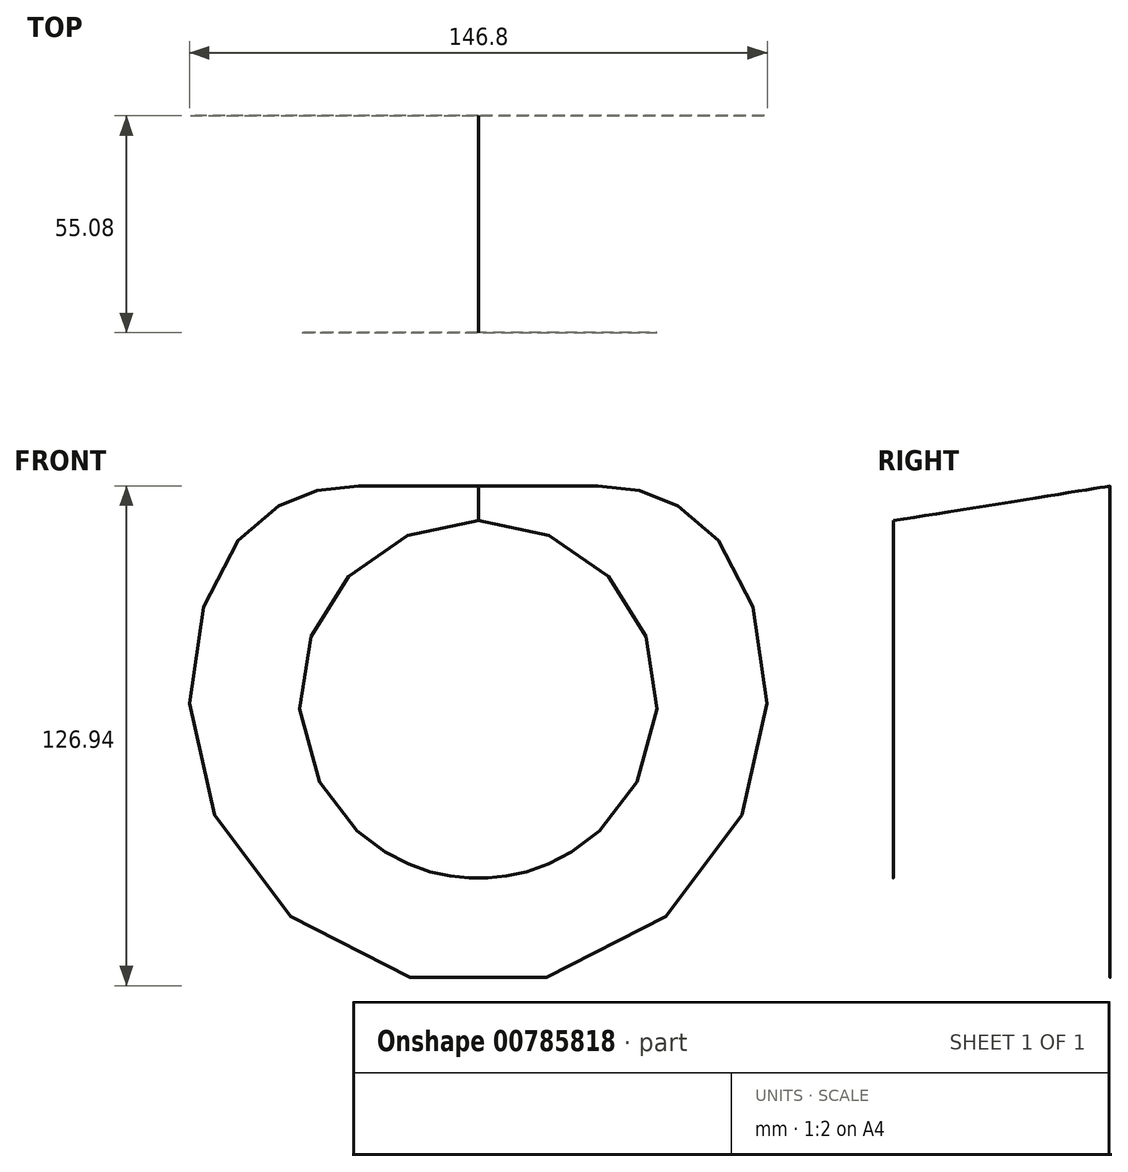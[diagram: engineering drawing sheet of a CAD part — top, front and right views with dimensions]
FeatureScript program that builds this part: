
annotation { "Feature Type Name" : "Feature", "Feature Type Description" : "" }
export const myFeature = defineFeature(function(context is Context, id is Id, definition is map)
    precondition{}
    {
        {
            var Q0;
            Q0=qCreatedBy(makeId("Front.planeOp"),FACE);
            cPlane(context, id + "F0", {"entities" : qUnion([Q0]), "cplaneType" : CPlaneType.OFFSET, "offset" : 50.8 * mm, "width" : 152.4 * mm, "height" : 152.4 * mm});
        }
        {
            var Q0;
            Q0=qCreatedBy(id+"F0.planeOp",FACE);
            var Q1;
            Q1 = qBodyType(qCreatedBy(id + "F2" ,EDGE), BodyType.WIRE);
            cPlane(context, id + "F1", {"entities" : qUnion([Q0, Q1]), "cplaneType" : CPlaneType.OFFSET, "offset" : 50.8 * mm, "width" : 152.4 * mm, "height" : 152.4 * mm});
        }
        {
            var Q0;
            Q0=qCreatedBy(id+"F1.planeOp",FACE);
            var sketch = newSketch(context, id + "F2", { "sketchPlane" : qUnion([Q0])});
            skCircle(sketch, "E0", {"center": v(0, 0) * mm, "radius": 91.15 * mm});
            skSolve(sketch);
        }
        {
            var Q0;
            Q0=qCreatedBy(id+"F1.planeOp",FACE);
            cPlane(context, id + "F3", {"entities" : qUnion([Q0]), "cplaneType" : CPlaneType.OFFSET, "offset" : 57.15 * mm, "width" : 152.4 * mm, "height" : 152.4 * mm});
        }
        {
            var Q0;
            Q0=qCreatedBy(id+"F3.planeOp",FACE);
            var sketch = newSketch(context, id + "F4", { "sketchPlane" : qUnion([Q0])});
            skArc(sketch, "E1", {"start": v(-65.98, 32.11) * mm, "mid": v(0, -73.38) * mm, "end": v(65.98, 32.11) * mm});
            skLineSegment(sketch, "E2", {"start": v(-31.72, 53.54) * mm, "end": v(0, 53.54) * mm});
            skLineSegment(sketch, "E3.MirrorCS", {"start": v(31.72, 53.54) * mm, "end": v(0, 53.54) * mm});
            skPoint(sketch, "E4.visualSharp", {"position": v(-50.18, 53.54) * mm});
            skArc(sketch, "E4.filletArc", {"start": v(-31.72, 53.54) * mm, "mid": v(-51.93, 47.74) * mm, "end": v(-65.98, 32.11) * mm});
            skPoint(sketch, "E5", {"position": v(50.18, 53.54) * mm});
            skArc(sketch, "E6.filletArc", {"start": v(65.98, 32.11) * mm, "mid": v(51.93, 47.74) * mm, "end": v(31.72, 53.54) * mm});
            skSolve(sketch);
        }
        {
            var Q0;
            Q0=qCreatedBy(id+"F3.planeOp",FACE);
            cPlane(context, id + "F5", {"entities" : qUnion([Q0]), "cplaneType" : CPlaneType.OFFSET, "offset" : 50.8 * mm, "width" : 152.4 * mm, "height" : 152.4 * mm});
        }
        {
            var Q0;
            Q0=qCreatedBy(id+"F5.planeOp",FACE);
            var sketch = newSketch(context, id + "F6", { "sketchPlane" : qUnion([Q0])});
            skCircle(sketch, "E7", {"center": v(0, 0) * mm, "radius": 45.44 * mm});
            skSolve(sketch);
        }
        {
            var Q0;
            Q0=qCreatedBy(id+"F5.planeOp",FACE);
            cPlane(context, id + "F7", {"entities" : qUnion([Q0]), "cplaneType" : CPlaneType.OFFSET, "offset" : 25.4 * mm, "width" : 152.4 * mm, "height" : 152.4 * mm});
        }
        {
            var Q0;
            Q0=qCreatedBy(makeId("Front.planeOp"),FACE);
            cPlane(context, id + "F8", {"entities" : qUnion([Q0]), "cplaneType" : CPlaneType.OFFSET, "offset" : 6.35 * mm, "oppositeDirection" : true, "width" : 152.4 * mm, "height" : 152.4 * mm});
        }
        {
            var Q0;
            Q0=qCreatedBy(makeId("Right.planeOp"),FACE);
            var sketch = newSketch(context, id + "F9", { "sketchPlane" : qUnion([Q0])});
            skLineSegment(sketch, "E8", {"start": v(-158.72, 53.54) * mm, "end": v(-213.8, 44.76) * mm});
            skLineSegment(sketch, "E9", {"start": v(-161.4, -71.92) * mm, "end": v(-212.9, -43.6) * mm});
            skSolve(sketch);
        }
        {
            var Q0;
            Q0=makeQuery(id+"F4.imprint","IMPRINT",FACE,{"disambiguationData":[TD([[makeQuery(id+"F4.imprint","IMPRINT",EDGE,{"derivedFrom":sQuery(id+"F4.wireOp",EDGE,"E1")}),1.0]])]});
            var Q1;
            Q1=makeQuery(id+"F6.imprint","IMPRINT",FACE,{"disambiguationData":[TD([[makeQuery(id+"F6.imprint","IMPRINT",EDGE,{"derivedFrom":sQuery(id+"F6.wireOp",EDGE,"E7")}),1.0]])]});
            var Q2;
            Q2=sQuery(id+"F9.wireOp",EDGE,"E8");
            loft(context, id + "F10", {"bodyType" : ToolBodyType.SURFACE, "addGuides" : true, "wireProfilesArray" : [{ "wireProfileEntities" : qUnion([Q0]) }, { "wireProfileEntities" : qUnion([Q1]) }], "guidesArray" : [{ "guideEntities" : qUnion([Q2]), "guideDerivativeType" : LoftGuideDerivativeType.DEFAULT, "guideDerivativeMagnitude" : 1 }]});
        }
    });
